# Revit family: 207_Uteluftkappe _ 00785
name_source: partatom
category: Air Terminals
revit_build: Autodesk Revit 2018 (Build: 20170223_1515(x64)
units: mm (PartAtom-declared; Revit-internal decimal feet)

## family parameters
Always vertical = Yes
Cut with Voids When Loaded = No
Part Type = Normal
Room Calculation Point = Yes
Round Connector Dimension = Use Diameter
Shared = No
Work Plane-Based = No

## types (1)
- 125-00785
    CAT0 = Yes
    CLBTZ = 0 mm  [stored 0 ft]
    CL_Location_5000 = 5000 mm  [stored 16.4042 ft]
    D = 125 mm
    Description = Air cowl exhaust/outdoor  male
    H1 = 130 mm  [stored 0.426509 ft]
    H_ARR = 0 mm  [stored 0 ft]
    L1 = 5 mm  [stored 0.0164042 ft]
    L2 = 190 mm  [stored 0.62336 ft]
    L_ARR = 400 mm  [stored 1.31234 ft]
    MC Product Code = 125-00785
    Manufacturer = Flexit
    QmdConnectorList = 201;D
    W2 = 180 mm  [stored 0.590551 ft]
    W_ARR = 400 mm  [stored 1.31234 ft]
    X2 = 90 mm  [stored 0.295276 ft]
    XRefLineVPlnId = 7453
    Y1 = 65 mm  [stored 0.213255 ft]
    YRefLineVPlnId = 7456
    Z1 = 40 mm  [stored 0.131234 ft]
    Z2 = 70 mm  [stored 0.229659 ft]
    Z3 = 45 mm  [stored 0.147638 ft]
    Z4 = 185 mm  [stored 0.606955 ft]
    Z5 = 95 mm  [stored 0.31168 ft]
    magiPartTypeId = 207
    magiProductFamilyId = Uteluftkappe * 00785
    magiProductId = Uteluftkappe 125

note: [stored X ft] marks values corroborated as IEEE doubles in the binary element streams (Revit-internal decimal feet)

## geometry (parser evidence)
native form markers: Sweep x2
no freeform markers — native parametric forms only
